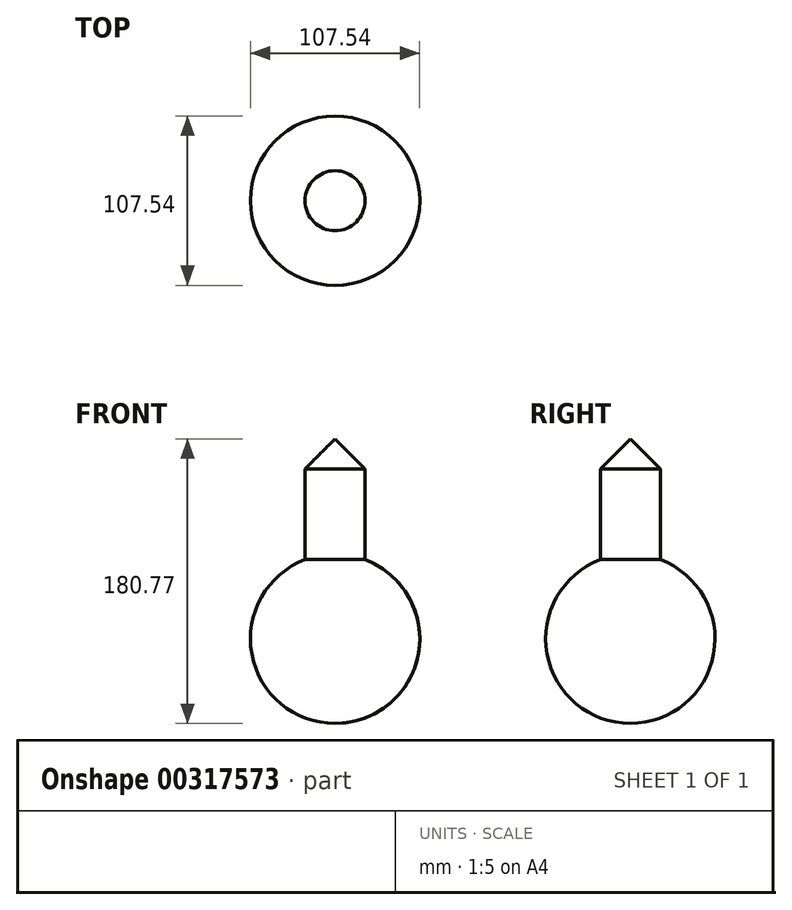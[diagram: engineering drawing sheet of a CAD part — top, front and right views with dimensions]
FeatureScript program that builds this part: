
annotation { "Feature Type Name" : "Feature", "Feature Type Description" : "" }
export const myFeature = defineFeature(function(context is Context, id is Id, definition is map)
    precondition{}
    {
        {
            var Q0;
            Q0=qCreatedBy(makeId("Front.planeOp"),FACE);
            var sketch = newSketch(context, id + "F0", { "sketchPlane" : qUnion([Q0])});
            skArc(sketch, "E0", {"start": v(0, 53.77) * mm, "mid": v(-53.77, 0) * mm, "end": v(0, -53.77) * mm});
            skLineSegment(sketch, "E1", {"start": v(0, 0) * mm, "end": v(0, 53.77) * mm});
            skLineSegment(sketch, "E2", {"start": v(0, 53.77) * mm, "end": v(0, 0) * mm});
            skLineSegment(sketch, "E3", {"start": v(0, -53.77) * mm, "end": v(0, 0) * mm});
            skSolve(sketch);
        }
        {
            var Q0;
            Q0=makeQuery(id+"F0.imprint","IMPRINT",FACE,{"disambiguationData":[TD([[makeQuery(id+"F0.imprint","IMPRINT",EDGE,{"derivedFrom":sQuery(id+"F0.wireOp",EDGE,"E0")}),1.0]])]});
            var Q1;
            Q1=sQuery(id+"F0.wireOp",EDGE,"E2");
            revolve(context, id + "F1", {"entities" : qUnion([Q0]), "axis" : qUnion([Q1]), "revolveType" : RevolveType.FULL});
        }
        {
            var Q0;
            Q0=qCreatedBy(makeId("Top.planeOp"),FACE);
            var sketch = newSketch(context, id + "F2", { "sketchPlane" : qUnion([Q0])});
            skCircle(sketch, "E4", {"center": v(0, 0) * mm, "radius": 19.05 * mm});
            skSolve(sketch);
        }
        {
            var Q0;
            Q0 = qSketchRegion(id + "F2", true);
            extrude(context, id + "F3", {"entities" : qUnion([Q0]), "operationType" : NewBodyOperationType.ADD, "oppositeDirection" : true, "depth" : 25.4 * mm});
        }
        {
            var Q0;
            Q0 = qSketchRegion(id + "F2", true);
            extrude(context, id + "F4", {"entities" : qUnion([Q0]), "operationType" : NewBodyOperationType.ADD, "depth" : 127 * mm});
        }
        {
            var Q0;
            Q0=makeQuery(id+"F4.opExtrude","CAP_EDGE",EDGE,{"disambiguationData":[OSD([sQuery(id+"F2.wireOp",EDGE,"E4")])],"isStart":false});
            chamfer(context, id + "F5", {"entities" : qUnion([Q0]), "width" : 19.05 * mm, "tangentPropagation" : true});
        }
    });
